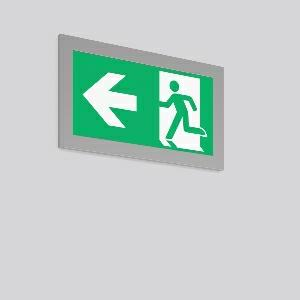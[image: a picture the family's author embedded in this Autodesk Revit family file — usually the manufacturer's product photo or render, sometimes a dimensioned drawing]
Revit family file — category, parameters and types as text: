
# Revit family: tenuo_671922_004_89_8fa4
name_source: partatom
category: Lighting Fixtures
units: mm (PartAtom-declared; Revit-internal decimal feet)

## family parameters
Cut with Voids When Loaded = No
Host = Face
Light Source = No
Part Type = Normal
Room Calculation Point = No
Round Connector Dimension = Use Diameter
Shared = No

## types (1)
- TENUO
    Apparent Load = 0 VA
    Default Elevation = 1800 mm
    Description = Series: TENUO
Luminaire for escape route identification. Housing: anodised aluminium, silver. Display panel: patented MicroLens technology and legend on one side. Driver integrated. Suitable for connection to central battery systems. With AC Control monitoring module for LUXIFAIR central battery units. Please indicate legend number when placing your order! 
Colour: silver, matt (approx. RAL 9006)
Length: 350 mm
Width: 11 mm
Height: 200 mm
Cut-out length: 175 mm
Cut-out width: 175 mm
Recess height: 70 mm
Luminaire: recess height: 55 mm
Weight: 1.99 kg
Operating mode: maintained power mode
Viewing Distance: 30 m
Lamp: LED
Socket: without socket
Colour temperature: 5700K
Colour rendering index (CRI): 80
System power: 4.8 W
System power, emergency: 4.8 W
Control gear: Regulated power supply
Protection class: I
Type of protection: IP 40
    Height = 200 mm  [stored 0.656168 ft]
    Lamp = 0 x
    Length = 350 mm
    Luminous efficacy = 0 lm/W
    Manufacturer = RZB
    ModVariant = No
    Model = 671922.004.89
    Mounting Place = Wall
    Mounting Type = Recessed
    Number of Poles = 1
    OnlyDefault = Yes
    Power Factor = 1
    Product Name = TENUO
    Product group = Recessed wall luminaires
    ProductGroupID = 2004
    Protection Class = Protection class I
    Protection Degree = IP 40
    RLX_Detail_Level = 1
    RLX_Emergency_Light_Flux = 0 lm
    RLX_Emergency_Type = 0
    RLX_Emergency_Type_DB = No
    RlxData = <blob elided: 25789 chars, md5=dec5e719>
    Standby Power = 0 W
    System Light Flux = 0 lm
    System Power = 0 W
    Type Comments = ALEA SPOT
    Type Image = 671922.004.jpg
    URL = http://relux.com
    VarID = ---
    Voltage = 230 V
    Voltage Range = 220-240 V
    Weight = 0.00 kg
    Width = 11 mm

note: [stored X ft] marks values corroborated as IEEE doubles in the binary element streams (Revit-internal decimal feet)

## geometry (parser evidence)
native form markers: Blend x4, Sweep x12
no freeform markers — native parametric forms only
